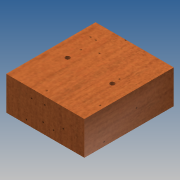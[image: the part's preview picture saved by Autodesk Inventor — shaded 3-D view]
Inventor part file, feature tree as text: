
AUTODESK INVENTOR PART (.ipt)
format: ipt  version: 2014 SP1 (Build 180222100, 222)  size: 118,784 bytes
history: native  units: in
note: dims shown in document units (in); Inventor stores cm internally (conversion verified against a paired STEP export)
features: sketch x3, hole x2, extrude x1
ambient origin geometry x8: Origin, YZ Plane, XZ Plane, XY Plane, X Axis, Y Axis, Z Axis, Center Point
bodies: Solid1 (feature_tree)
feature tree (6):
  extrude  "Extrusion1"  Depth=1.5in
  hole  "Hole1"  [1 undecoded]
  hole  "Hole3"  [1 undecoded]
  sketch  "Sketch1"  dims[d0=3.5in d1=1.5in]
  sketch  "Sketch3"  dims[d2=4.0in d3=0.0in d4=0.75in]
  sketch  "Sketch4"  dims[d5=0.201in d6=0.75in d7=0.385in d8=0.25in d9=0.5635in d10=1.0in d11=0.8108in d12=0.75in d13=0.5in d21=0.201in d22=0.75in d23=0.385in d24=0.25in d25=0.5635in d26=1.0in d27=0.8108in]
note: 2 required parameter values undecoded (feature->parameter linkage not recoverable at this tier; creation-order binding heuristic only, values carry confidence <= 0.55)
